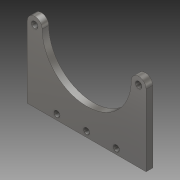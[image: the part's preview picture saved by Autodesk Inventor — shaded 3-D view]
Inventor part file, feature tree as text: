
AUTODESK INVENTOR PART (.ipt)
format: ipt  version: 2019 (Build 230136000, 136)  size: 109,056 bytes
history: native  units: mm
features: extrude x1, sketch x1
ambient origin geometry x8: Origin, YZ Plane, XZ Plane, XY Plane, X Axis, Y Axis, Z Axis, Center Point
bodies: Body1 (feature_tree)
feature tree (2):
  extrude  "Extrusion2"  Depth=6.0mm
  sketch  "Sketch1"  dims[d0=108.0mm d2=6.0mm d3=6.0mm d6=94.5mm d9=65.0mm d21=5.0mm d23=5.5mm d24=5.5mm d25=5.5mm d26=54.0mm d27=6.0mm d28=0.0mm]
